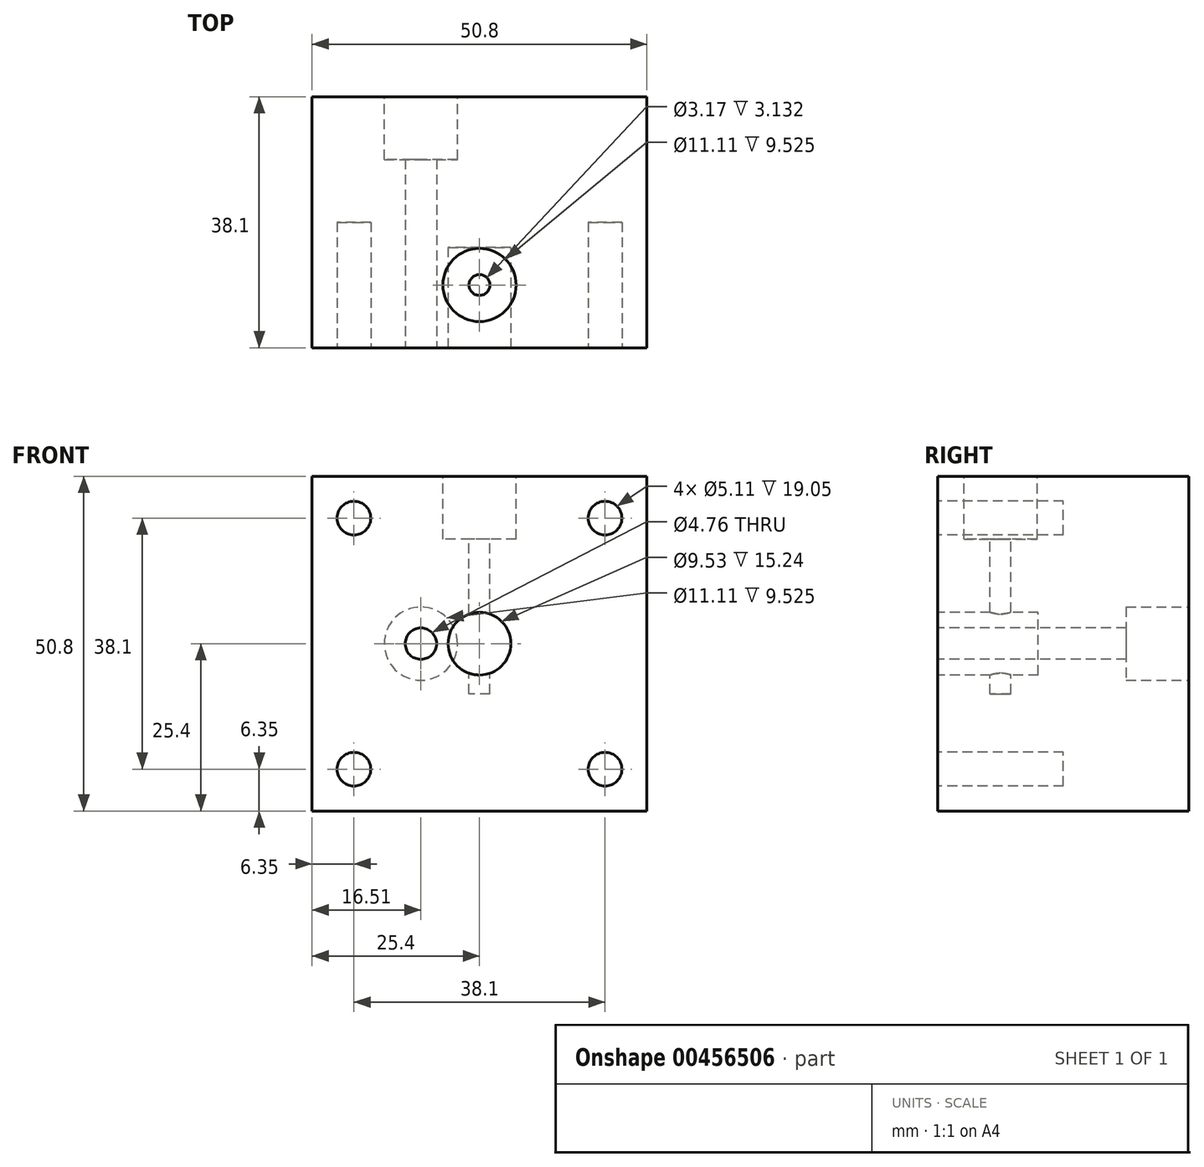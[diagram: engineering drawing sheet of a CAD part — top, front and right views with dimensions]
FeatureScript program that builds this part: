
annotation { "Feature Type Name" : "Feature", "Feature Type Description" : "" }
export const myFeature = defineFeature(function(context is Context, id is Id, definition is map)
    precondition{}
    {
        {
            var Q0;
            Q0=qCreatedBy(makeId("Front.planeOp"),FACE);
            var sketch = newSketch(context, id + "F0", { "sketchPlane" : qUnion([Q0])});
            skLineSegment(sketch, "E0.bottom", {"start": v(25.4, 25.4) * mm, "end": v(-25.4, 25.4) * mm});
            skLineSegment(sketch, "E0.top", {"start": v(25.4, -25.4) * mm, "end": v(-25.4, -25.4) * mm});
            skLineSegment(sketch, "E0.left", {"start": v(25.4, 25.4) * mm, "end": v(25.4, -25.4) * mm});
            skLineSegment(sketch, "E0.right", {"start": v(-25.4, 25.4) * mm, "end": v(-25.4, -25.4) * mm});
            skPoint(sketch, "E0.middle", {"position": v(0, 0) * mm});
            skSolve(sketch);
        }
        {
            var Q0;
            Q0=qSketchRegion(id+"F0",true);
            extrude(context, id + "F1", {"entities" : qUnion([Q0]), "endBound" : BoundingType.SYMMETRIC, "depth" : 38.1 * mm});
        }
        {
            var Q0;
            Q0=makeQuery(id+"F1.opExtrude","CAP_FACE",FACE,{"disambiguationData":[OSD([sQuery(id+"F0.wireOp",EDGE,"E0.bottom"),sQuery(id+"F0.wireOp",EDGE,"E0.top"),sQuery(id+"F0.wireOp",EDGE,"E0.left"),sQuery(id+"F0.wireOp",EDGE,"E0.right")])],"isStart":false});
            var sketch = newSketch(context, id + "F2", { "sketchPlane" : qUnion([Q0])});
            skLineSegment(sketch, "E1", {"start": v(-3.5, 2.83) * mm, "end": v(3.5, -2.83) * mm, "construction": true});
            skLineSegment(sketch, "E2", {"start": v(3.5, 2.83) * mm, "end": v(-3.5, -2.83) * mm, "construction": true});
            skCircle(sketch, "E3", {"center": v(0, 0) * mm, "radius": 12.7 * mm, "construction": true});
            skLineSegment(sketch, "E4", {"start": v(-3.5, 2.83) * mm, "end": v(-3.5, -2.83) * mm, "construction": true});
            skLineSegment(sketch, "E5", {"start": v(3.5, 2.83) * mm, "end": v(3.5, -2.83) * mm, "construction": true});
            skArc(sketch, "E6", {"start": v(-3.5, 2.83) * mm, "mid": v(0, 4.5) * mm, "end": v(3.5, 2.83) * mm, "construction": true});
            skArc(sketch, "E7", {"start": v(-3.5, -2.83) * mm, "mid": v(0, -4.5) * mm, "end": v(3.5, -2.83) * mm, "construction": true});
            skCircle(sketch, "E8", {"center": v(0, 0) * mm, "radius": 4.5 * mm, "construction": true});
            skCircle(sketch, "E9", {"center": v(0, 0) * mm, "radius": 4.76 * mm});
            skSolve(sketch);
        }
        {
            var Q0;
            Q0=qSketchRegion(id+"F2",true);
            extrude(context, id + "F3", {"entities" : qUnion([Q0]), "operationType" : NewBodyOperationType.REMOVE, "oppositeDirection" : true, "depth" : 15.24 * mm});
        }
        {
            var Q0;
            Q0=makeQuery(id+"F1.opExtrude","SWEPT_FACE",FACE,{"disambiguationData":[OSD([sQuery(id+"F0.wireOp",EDGE,"E0.bottom")])]});
            var sketch = newSketch(context, id + "F4", { "sketchPlane" : qUnion([Q0])});
            skCircle(sketch, "E10", {"center": v(0, -9.53) * mm, "radius": 1.59 * mm});
            skSolve(sketch);
        }
        {
            var Q0;
            Q0=qSketchRegion(id+"F4",true);
            extrude(context, id + "F5", {"entities" : qUnion([Q0]), "operationType" : NewBodyOperationType.REMOVE, "oppositeDirection" : true, "depth" : 33.02 * mm});
        }
        {
            var Q0;
            Q0=makeQuery(id+"F1.opExtrude","SWEPT_FACE",FACE,{"disambiguationData":[OSD([sQuery(id+"F0.wireOp",EDGE,"E0.bottom")])]});
            var sketch = newSketch(context, id + "F6", { "sketchPlane" : qUnion([Q0])});
            skCircle(sketch, "E11", {"center": v(0, -9.53) * mm, "radius": 5.56 * mm});
            skSolve(sketch);
        }
        {
            var Q0;
            Q0=qSketchRegion(id+"F6",true);
            extrude(context, id + "F7", {"entities" : qUnion([Q0]), "operationType" : NewBodyOperationType.REMOVE, "oppositeDirection" : true, "depth" : 9.52 * mm});
        }
        {
            var Q0;
            Q0=makeQuery(id+"F1.opExtrude","CAP_FACE",FACE,{"disambiguationData":[OSD([sQuery(id+"F0.wireOp",EDGE,"E0.bottom"),sQuery(id+"F0.wireOp",EDGE,"E0.top"),sQuery(id+"F0.wireOp",EDGE,"E0.left"),sQuery(id+"F0.wireOp",EDGE,"E0.right")])],"isStart":false});
            var sketch = newSketch(context, id + "F8", { "sketchPlane" : qUnion([Q0])});
            skCircle(sketch, "E12", {"center": v(-8.9, 0) * mm, "radius": 2.38 * mm});
            skSolve(sketch);
        }
        {
            var Q0;
            Q0=qSketchRegion(id+"F8",true);
            extrude(context, id + "F9", {"entities" : qUnion([Q0]), "operationType" : NewBodyOperationType.REMOVE, "endBound" : BoundingType.UP_TO_NEXT, "oppositeDirection" : true, "depth" : 25.4 * mm});
        }
        {
            var Q0;
            Q0=makeQuery(id+"F1.opExtrude","CAP_FACE",FACE,{"disambiguationData":[OSD([sQuery(id+"F0.wireOp",EDGE,"E0.bottom"),sQuery(id+"F0.wireOp",EDGE,"E0.top"),sQuery(id+"F0.wireOp",EDGE,"E0.left"),sQuery(id+"F0.wireOp",EDGE,"E0.right")])],"isStart":true});
            var sketch = newSketch(context, id + "F10", { "sketchPlane" : qUnion([Q0])});
            skCircle(sketch, "E13", {"center": v(8.9, 0) * mm, "radius": 5.56 * mm});
            skSolve(sketch);
        }
        {
            var Q0;
            Q0=qSketchRegion(id+"F10",true);
            extrude(context, id + "F11", {"entities" : qUnion([Q0]), "operationType" : NewBodyOperationType.REMOVE, "oppositeDirection" : true, "depth" : 9.52 * mm});
        }
        {
            var Q0;
            Q0=makeQuery(id+"F2.imprint","IMPRINT",FACE,{"disambiguationData":[TD([[makeQuery(id+"F2.imprint","IMPRINT",EDGE,{"derivedFrom":sQuery(id+"F2.wireOp",EDGE,"E9")}),-1.0]])]});
            var sketch = newSketch(context, id + "F12", { "sketchPlane" : qUnion([Q0])});
            skCircle(sketch, "E14", {"center": v(-19.05, 19.05) * mm, "radius": 2.55 * mm});
            skCircle(sketch, "E15.MirrorC", {"center": v(19.05, 19.05) * mm, "radius": 2.55 * mm});
            skCircle(sketch, "E16.MirrorC", {"center": v(-19.05, -19.05) * mm, "radius": 2.55 * mm});
            skCircle(sketch, "E17.MirrorC", {"center": v(19.05, -19.05) * mm, "radius": 2.55 * mm});
            skSolve(sketch);
        }
        {
            var Q0;
            Q0=qSketchRegion(id+"F12",true);
            extrude(context, id + "F13", {"entities" : qUnion([Q0]), "operationType" : NewBodyOperationType.REMOVE, "oppositeDirection" : true, "depth" : 19.05 * mm});
        }
    });
